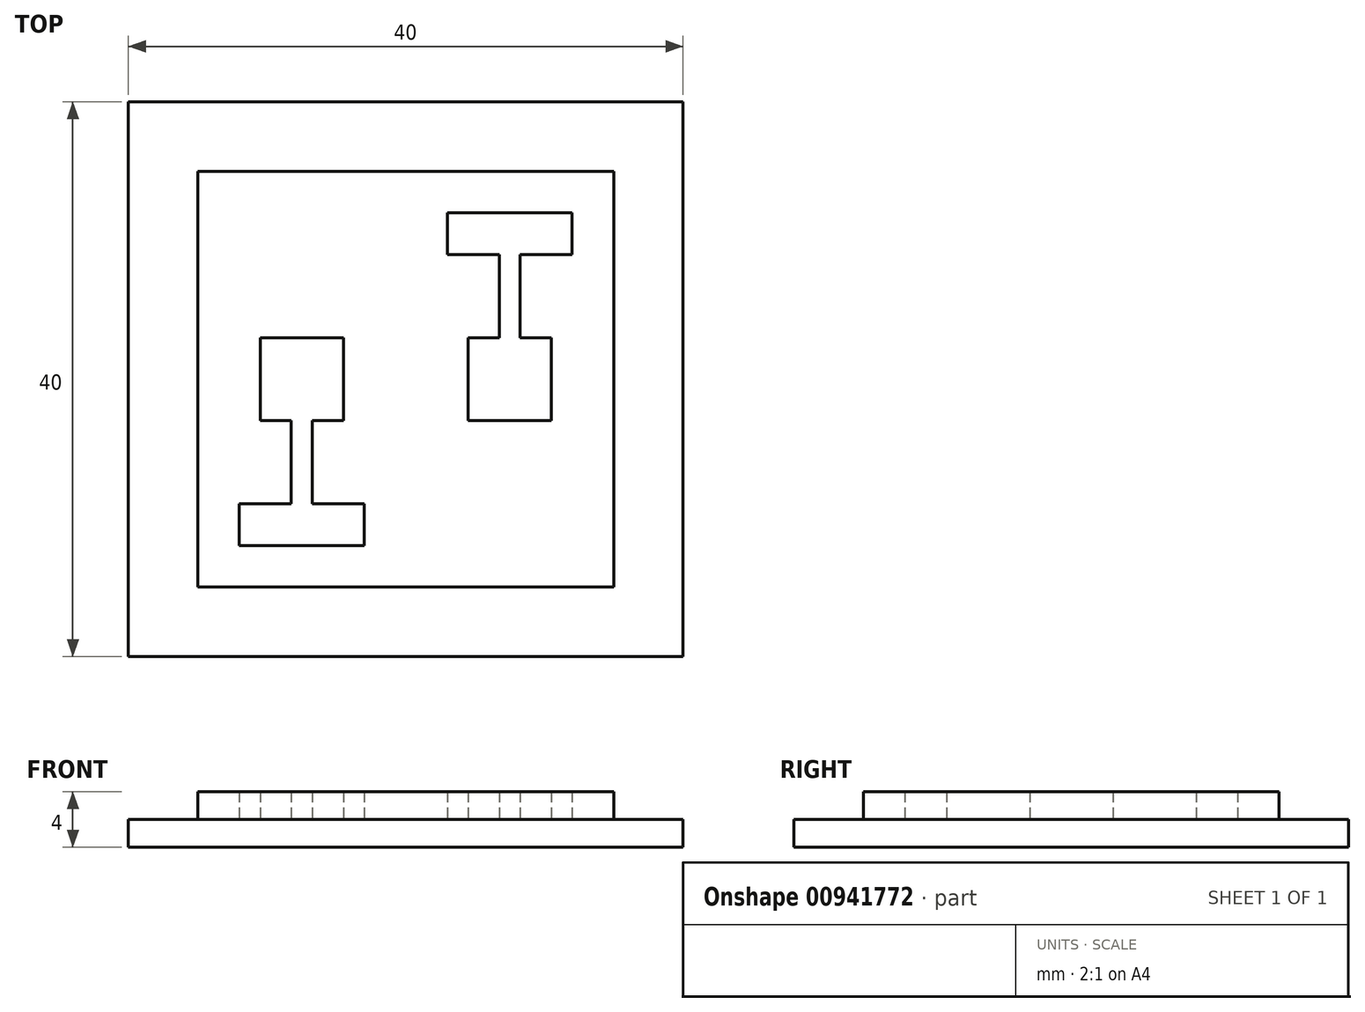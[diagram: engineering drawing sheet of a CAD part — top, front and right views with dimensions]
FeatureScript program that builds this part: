
annotation { "Feature Type Name" : "Feature", "Feature Type Description" : "" }
export const myFeature = defineFeature(function(context is Context, id is Id, definition is map)
    precondition{}
    {
        {
            var Q0;
            Q0=qCreatedBy(makeId("Top.planeOp"),FACE);
            var sketch = newSketch(context, id + "F0", { "sketchPlane" : qUnion([Q0])});
            skLineSegment(sketch, "E0.bottom", {"start": v(-20, 20) * mm, "end": v(20, 20) * mm});
            skLineSegment(sketch, "E0.top", {"start": v(-20, -20) * mm, "end": v(20, -20) * mm});
            skLineSegment(sketch, "E0.left", {"start": v(-20, 20) * mm, "end": v(-20, -20) * mm});
            skLineSegment(sketch, "E0.right", {"start": v(20, 20) * mm, "end": v(20, -20) * mm});
            skPoint(sketch, "E0.middle", {"position": v(0, 0) * mm});
            skSolve(sketch);
        }
        {
            var Q0;
            Q0 = qSketchRegion(id + "F0", true);
            extrude(context, id + "F1", {"entities" : qUnion([Q0]), "depth" : 2 * mm, "offsetDistance" : 25.4 * mm});
        }
        {
            var Q0;
            Q0=makeQuery(id+"F1.opExtrude","CAP_FACE",FACE,{"disambiguationData":[OSD([sQuery(id+"F0.wireOp",EDGE,"E0.bottom"),sQuery(id+"F0.wireOp",EDGE,"E0.top"),sQuery(id+"F0.wireOp",EDGE,"E0.left"),sQuery(id+"F0.wireOp",EDGE,"E0.right")])],"isStart":false});
            var sketch = newSketch(context, id + "F2", { "sketchPlane" : qUnion([Q0])});
            skPoint(sketch, "E1", {"position": v(-8.25, -3) * mm});
            skLineSegment(sketch, "E2.left", {"start": v(-8.25, -3) * mm, "end": v(-8.25, -9) * mm});
            skLineSegment(sketch, "E2.right", {"start": v(-6.75, -3) * mm, "end": v(-6.75, -9) * mm});
            skLineSegment(sketch, "E3.top", {"start": v(-12, -12) * mm, "end": v(-3, -12) * mm});
            skLineSegment(sketch, "E3.left", {"start": v(-12, -9) * mm, "end": v(-12, -12) * mm});
            skLineSegment(sketch, "E3.right", {"start": v(-3, -9) * mm, "end": v(-3, -12) * mm});
            skLineSegment(sketch, "E4.top", {"start": v(-4.5, 3) * mm, "end": v(-10.5, 3) * mm});
            skLineSegment(sketch, "E4.left", {"start": v(-4.5, -3) * mm, "end": v(-4.5, 3) * mm});
            skLineSegment(sketch, "E4.right", {"start": v(-10.5, -3) * mm, "end": v(-10.5, 3) * mm});
            skPoint(sketch, "E4.middle", {"position": v(-7.5, 0) * mm});
            skLineSegment(sketch, "E5.MirrorCS", {"start": v(8.25, -3) * mm, "end": v(6.75, -3) * mm});
            skLineSegment(sketch, "E6.MirrorCS", {"start": v(10.5, -3) * mm, "end": v(10.5, 3) * mm});
            skPoint(sketch, "E7.MirrorP", {"position": v(7.5, 0) * mm});
            skLineSegment(sketch, "E8.MirrorCS", {"start": v(4.5, -3) * mm, "end": v(10.5, -3) * mm});
            skLineSegment(sketch, "E9.MirrorCS", {"start": v(4.5, -3) * mm, "end": v(4.5, 3) * mm});
            skLineSegment(sketch, "E10", {"start": v(-12, -9) * mm, "end": v(-8.25, -9) * mm});
            skLineSegment(sketch, "E11", {"start": v(-6.75, -9) * mm, "end": v(-3, -9) * mm});
            skLineSegment(sketch, "E12", {"start": v(-10.5, -3) * mm, "end": v(-8.25, -3) * mm});
            skLineSegment(sketch, "E13", {"start": v(-6.75, -3) * mm, "end": v(-4.5, -3) * mm});
            skLineSegment(sketch, "E14.left", {"start": v(6.75, 9) * mm, "end": v(6.75, 3) * mm});
            skLineSegment(sketch, "E14.right", {"start": v(8.25, 9) * mm, "end": v(8.25, 3) * mm});
            skLineSegment(sketch, "E15.bottom", {"start": v(3, 12) * mm, "end": v(12, 12) * mm});
            skLineSegment(sketch, "E15.left", {"start": v(3, 12) * mm, "end": v(3, 9) * mm});
            skLineSegment(sketch, "E15.right", {"start": v(12, 12) * mm, "end": v(12, 9) * mm});
            skLineSegment(sketch, "E16", {"start": v(3, 9) * mm, "end": v(6.75, 9) * mm});
            skLineSegment(sketch, "E17", {"start": v(8.25, 9) * mm, "end": v(12, 9) * mm});
            skLineSegment(sketch, "E18", {"start": v(4.5, 3) * mm, "end": v(6.75, 3) * mm});
            skLineSegment(sketch, "E19", {"start": v(8.25, 3) * mm, "end": v(10.5, 3) * mm});
            skPoint(sketch, "E20.middle", {"position": v(0, 0) * mm});
            skLineSegment(sketch, "E21.bottom", {"start": v(-15, 15) * mm, "end": v(15, 15) * mm});
            skLineSegment(sketch, "E21.top", {"start": v(-15, -15) * mm, "end": v(15, -15) * mm});
            skLineSegment(sketch, "E21.left", {"start": v(-15, 15) * mm, "end": v(-15, -15) * mm});
            skLineSegment(sketch, "E21.right", {"start": v(15, 15) * mm, "end": v(15, -15) * mm});
            skSolve(sketch);
        }
        {
            var Q0;
            Q0 = qSketchRegion(id + "F2", true);
            extrude(context, id + "F3", {"entities" : qUnion([Q0]), "operationType" : NewBodyOperationType.ADD, "depth" : 2 * mm, "offsetDistance" : 25.4 * mm});
        }
    });
